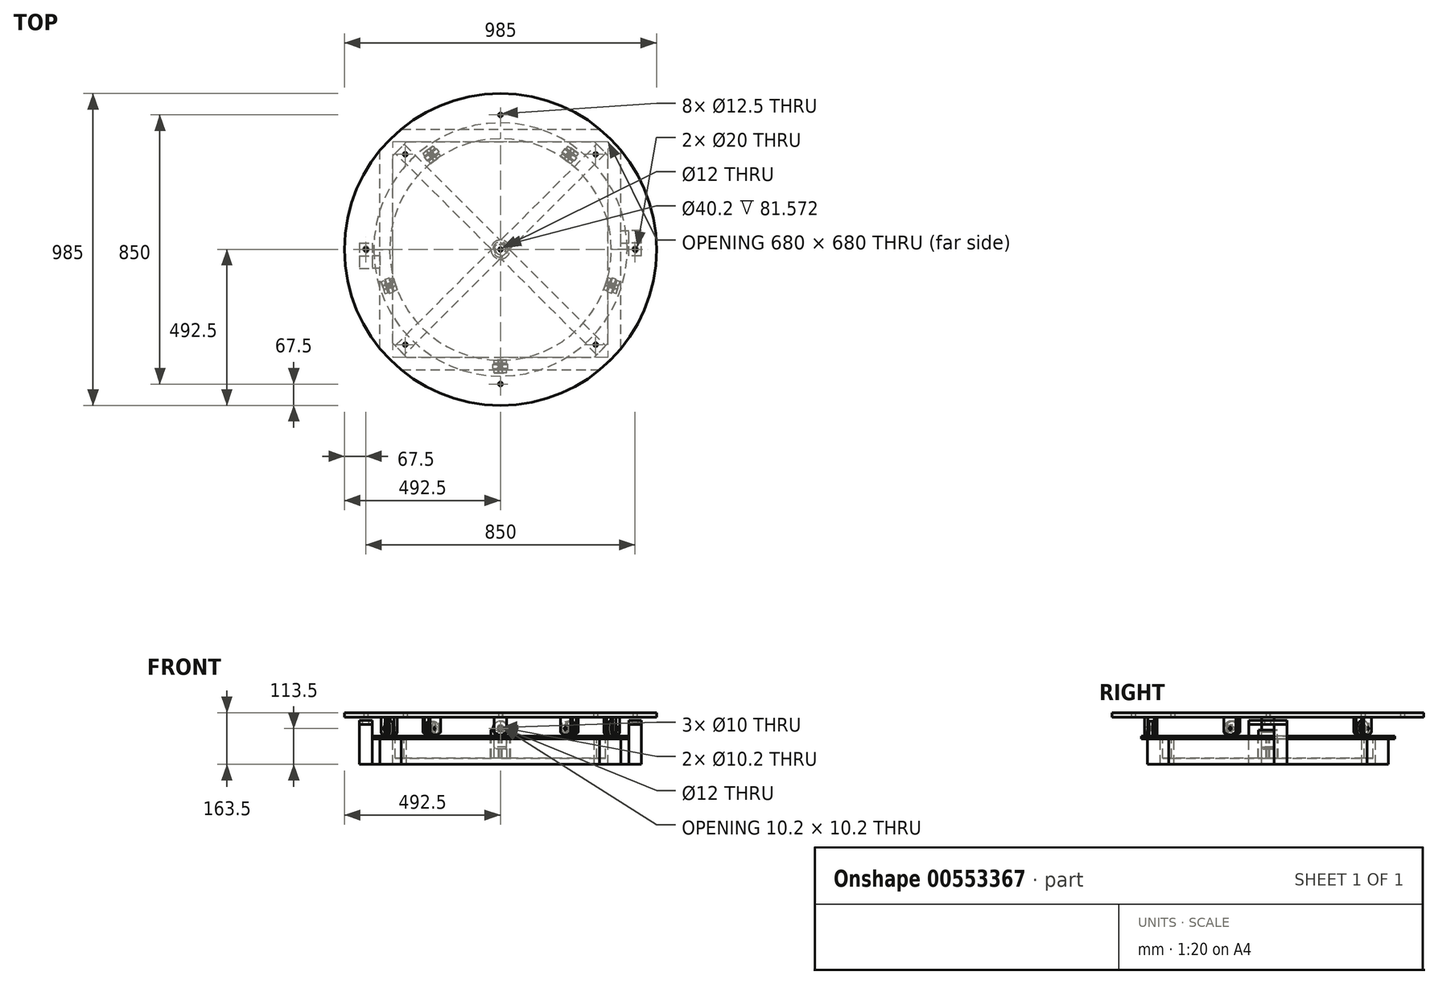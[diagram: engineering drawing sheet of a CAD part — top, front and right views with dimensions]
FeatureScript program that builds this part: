
annotation { "Feature Type Name" : "Feature", "Feature Type Description" : "" }
export const myFeature = defineFeature(function(context is Context, id is Id, definition is map)
    precondition{}
    {
        {
            var Q0;
            Q0=qCreatedBy(makeId("Top.planeOp"),FACE);
            var sketch = newSketch(context, id + "F0", { "sketchPlane" : qUnion([Q0])});
            skCircle(sketch, "E0", {"center": v(0, 0) * mm, "radius": 492.5 * mm});
            skCircle(sketch, "E1", {"center": v(0, -425) * mm, "radius": 6.25 * mm});
            skCircle(sketch, "E2.1.0", {"center": v(300.52, -300.52) * mm, "radius": 6.25 * mm});
            skCircle(sketch, "E2.2.0", {"center": v(425, 0) * mm, "radius": 6.25 * mm});
            skCircle(sketch, "E2.3.0", {"center": v(300.52, 300.52) * mm, "radius": 6.25 * mm});
            skCircle(sketch, "E2.4.0", {"center": v(0, 425) * mm, "radius": 6.25 * mm});
            skCircle(sketch, "E2.5.0", {"center": v(-300.52, 300.52) * mm, "radius": 6.25 * mm});
            skCircle(sketch, "E2.6.0", {"center": v(-425, 0) * mm, "radius": 6.25 * mm});
            skCircle(sketch, "E2.7.0", {"center": v(-300.52, -300.52) * mm, "radius": 6.25 * mm});
            skCircle(sketch, "E3", {"center": v(0, 0) * mm, "radius": 6 * mm});
            skSolve(sketch);
        }
        {
            var Q0;
            Q0 = qSketchRegion(id + "F0", true);
            extrude(context, id + "F1", {"entities" : qUnion([Q0]), "depth" : 15 * mm, "offsetDistance" : 25 * mm});
        }
        {
            var Q0;
            Q0=makeQuery(id+"F1.opExtrude","CAP_FACE",FACE,{"disambiguationData":[OSD([sQuery(id+"F0.wireOp",EDGE,"E0"),sQuery(id+"F0.wireOp",EDGE,"E1"),sQuery(id+"F0.wireOp",EDGE,"E2.1.0"),sQuery(id+"F0.wireOp",EDGE,"E2.2.0"),sQuery(id+"F0.wireOp",EDGE,"E2.3.0"),sQuery(id+"F0.wireOp",EDGE,"E2.4.0"),sQuery(id+"F0.wireOp",EDGE,"E2.5.0"),sQuery(id+"F0.wireOp",EDGE,"E2.6.0"),sQuery(id+"F0.wireOp",EDGE,"E2.7.0"),sQuery(id+"F0.wireOp",EDGE,"E3")])],"isStart":true});
            var sketch = newSketch(context, id + "F2", { "sketchPlane" : qUnion([Q0])});
            skCircle(sketch, "E4", {"center": v(0, 0) * mm, "radius": 390 * mm});
            skLineSegment(sketch, "E5", {"start": v(0, 389.49) * mm, "end": v(-20, 389.49) * mm});
            skLineSegment(sketch, "E6", {"start": v(0, 379.49) * mm, "end": v(-20, 379.49) * mm});
            skLineSegment(sketch, "E7", {"start": v(-20, 379.49) * mm, "end": v(-20, 389.49) * mm});
            skLineSegment(sketch, "E8.MirrorCS", {"start": v(0, 389.49) * mm, "end": v(20, 389.49) * mm});
            skLineSegment(sketch, "E9.MirrorCS", {"start": v(20, 379.49) * mm, "end": v(20, 399.5) * mm});
            skLineSegment(sketch, "E10.MirrorCS", {"start": v(0, 379.49) * mm, "end": v(20, 379.49) * mm});
            skLineSegment(sketch, "E11.0.1.0", {"start": v(0, 349.49) * mm, "end": v(20, 349.49) * mm});
            skLineSegment(sketch, "E11.0.1.1", {"start": v(20, 349.49) * mm, "end": v(20, 369.5) * mm});
            skLineSegment(sketch, "E11.0.1.2", {"start": v(0, 359.49) * mm, "end": v(20, 359.49) * mm});
            skLineSegment(sketch, "E11.0.1.3", {"start": v(0, 359.49) * mm, "end": v(-20, 359.49) * mm});
            skLineSegment(sketch, "E11.0.1.4", {"start": v(-20, 349.49) * mm, "end": v(-20, 359.49) * mm});
            skLineSegment(sketch, "E11.0.1.5", {"start": v(0, 349.49) * mm, "end": v(-20, 349.49) * mm});
            skLineSegment(sketch, "E11.direction1", {"start": v(0, 379.49) * mm, "end": v(15.32, 379.49) * mm, "construction": true});
            skLineSegment(sketch, "E11.direction2", {"start": v(0, 379.49) * mm, "end": v(0, 349.49) * mm, "construction": true});
            skLineSegment(sketch, "E12.1.0", {"start": v(-354.73, 136.29) * mm, "end": v(-373.77, 142.47) * mm});
            skLineSegment(sketch, "E12.1.1", {"start": v(-370.42, 120.36) * mm, "end": v(-364.24, 139.38) * mm});
            skLineSegment(sketch, "E12.1.2", {"start": v(-370.42, 120.36) * mm, "end": v(-376.6, 101.34) * mm});
            skLineSegment(sketch, "E12.1.3", {"start": v(-367.1, 98.25) * mm, "end": v(-376.6, 101.34) * mm});
            skLineSegment(sketch, "E12.1.4", {"start": v(-360.91, 117.27) * mm, "end": v(-367.1, 98.25) * mm});
            skLineSegment(sketch, "E12.1.5", {"start": v(-360.91, 117.27) * mm, "end": v(-356.18, 131.84) * mm, "construction": true});
            skLineSegment(sketch, "E12.1.6", {"start": v(-360.91, 117.27) * mm, "end": v(-332.38, 108) * mm, "construction": true});
            skLineSegment(sketch, "E12.1.7", {"start": v(-332.38, 108) * mm, "end": v(-326.2, 127.02) * mm});
            skLineSegment(sketch, "E12.1.8", {"start": v(-332.38, 108) * mm, "end": v(-338.56, 88.98) * mm});
            skLineSegment(sketch, "E12.1.9", {"start": v(-338.56, 88.98) * mm, "end": v(-348.07, 92.07) * mm});
            skLineSegment(sketch, "E12.1.10", {"start": v(-341.9, 111.09) * mm, "end": v(-348.07, 92.07) * mm});
            skLineSegment(sketch, "E12.1.11", {"start": v(-341.9, 111.09) * mm, "end": v(-335.71, 130.1) * mm});
            skLineSegment(sketch, "E12.1.12", {"start": v(-326.2, 127.02) * mm, "end": v(-345.23, 133.2) * mm});
            skLineSegment(sketch, "E12.1.13", {"start": v(-360.91, 117.27) * mm, "end": v(-354.73, 136.29) * mm});
            skLineSegment(sketch, "E12.2.0", {"start": v(-239.24, -295.26) * mm, "end": v(-251, -311.45) * mm});
            skLineSegment(sketch, "E12.2.1", {"start": v(-228.93, -315.1) * mm, "end": v(-245.11, -303.35) * mm});
            skLineSegment(sketch, "E12.2.2", {"start": v(-228.93, -315.1) * mm, "end": v(-212.75, -326.86) * mm});
            skLineSegment(sketch, "E12.2.3", {"start": v(-206.88, -318.77) * mm, "end": v(-212.75, -326.86) * mm});
            skLineSegment(sketch, "E12.2.4", {"start": v(-223.06, -307.01) * mm, "end": v(-206.88, -318.77) * mm});
            skLineSegment(sketch, "E12.2.5", {"start": v(-223.06, -307.01) * mm, "end": v(-235.45, -298) * mm, "construction": true});
            skLineSegment(sketch, "E12.2.6", {"start": v(-223.06, -307.01) * mm, "end": v(-205.42, -282.74) * mm, "construction": true});
            skLineSegment(sketch, "E12.2.7", {"start": v(-205.42, -282.74) * mm, "end": v(-221.6, -270.99) * mm});
            skLineSegment(sketch, "E12.2.8", {"start": v(-205.42, -282.74) * mm, "end": v(-189.24, -294.5) * mm});
            skLineSegment(sketch, "E12.2.9", {"start": v(-189.24, -294.5) * mm, "end": v(-195.12, -302.59) * mm});
            skLineSegment(sketch, "E12.2.10", {"start": v(-211.3, -290.83) * mm, "end": v(-195.12, -302.59) * mm});
            skLineSegment(sketch, "E12.2.11", {"start": v(-211.3, -290.83) * mm, "end": v(-227.48, -279.08) * mm});
            skLineSegment(sketch, "E12.2.12", {"start": v(-221.6, -270.99) * mm, "end": v(-233.37, -287.18) * mm});
            skLineSegment(sketch, "E12.2.13", {"start": v(-223.06, -307.01) * mm, "end": v(-239.24, -295.26) * mm});
            skLineSegment(sketch, "E12.3.0", {"start": v(206.88, -318.77) * mm, "end": v(218.64, -334.96) * mm});
            skLineSegment(sketch, "E12.3.1", {"start": v(228.93, -315.1) * mm, "end": v(212.75, -326.86) * mm});
            skLineSegment(sketch, "E12.3.2", {"start": v(228.93, -315.1) * mm, "end": v(245.11, -303.35) * mm});
            skLineSegment(sketch, "E12.3.3", {"start": v(239.24, -295.26) * mm, "end": v(245.11, -303.35) * mm});
            skLineSegment(sketch, "E12.3.4", {"start": v(223.06, -307.01) * mm, "end": v(239.24, -295.26) * mm});
            skLineSegment(sketch, "E12.3.5", {"start": v(223.06, -307.01) * mm, "end": v(210.66, -316.02) * mm, "construction": true});
            skLineSegment(sketch, "E12.3.6", {"start": v(223.06, -307.01) * mm, "end": v(205.42, -282.74) * mm, "construction": true});
            skLineSegment(sketch, "E12.3.7", {"start": v(205.42, -282.74) * mm, "end": v(189.24, -294.5) * mm});
            skLineSegment(sketch, "E12.3.8", {"start": v(205.42, -282.74) * mm, "end": v(221.6, -270.99) * mm});
            skLineSegment(sketch, "E12.3.9", {"start": v(221.6, -270.99) * mm, "end": v(227.48, -279.08) * mm});
            skLineSegment(sketch, "E12.3.10", {"start": v(211.3, -290.83) * mm, "end": v(227.48, -279.08) * mm});
            skLineSegment(sketch, "E12.3.11", {"start": v(211.3, -290.83) * mm, "end": v(195.12, -302.59) * mm});
            skLineSegment(sketch, "E12.3.12", {"start": v(189.24, -294.5) * mm, "end": v(201, -310.69) * mm});
            skLineSegment(sketch, "E12.3.13", {"start": v(223.06, -307.01) * mm, "end": v(206.88, -318.77) * mm});
            skLineSegment(sketch, "E12.4.0", {"start": v(367.1, 98.25) * mm, "end": v(386.13, 104.43) * mm});
            skLineSegment(sketch, "E12.4.1", {"start": v(370.42, 120.36) * mm, "end": v(376.6, 101.34) * mm});
            skLineSegment(sketch, "E12.4.2", {"start": v(370.42, 120.36) * mm, "end": v(364.24, 139.38) * mm});
            skLineSegment(sketch, "E12.4.3", {"start": v(354.73, 136.29) * mm, "end": v(364.24, 139.38) * mm});
            skLineSegment(sketch, "E12.4.4", {"start": v(360.91, 117.27) * mm, "end": v(354.73, 136.29) * mm});
            skLineSegment(sketch, "E12.4.5", {"start": v(360.91, 117.27) * mm, "end": v(365.65, 102.7) * mm, "construction": true});
            skLineSegment(sketch, "E12.4.6", {"start": v(360.91, 117.27) * mm, "end": v(332.38, 108) * mm, "construction": true});
            skLineSegment(sketch, "E12.4.7", {"start": v(332.38, 108) * mm, "end": v(338.56, 88.98) * mm});
            skLineSegment(sketch, "E12.4.8", {"start": v(332.38, 108) * mm, "end": v(326.2, 127.02) * mm});
            skLineSegment(sketch, "E12.4.9", {"start": v(326.2, 127.02) * mm, "end": v(335.71, 130.1) * mm});
            skLineSegment(sketch, "E12.4.10", {"start": v(341.9, 111.09) * mm, "end": v(335.71, 130.1) * mm});
            skLineSegment(sketch, "E12.4.11", {"start": v(341.9, 111.09) * mm, "end": v(348.07, 92.07) * mm});
            skLineSegment(sketch, "E12.4.12", {"start": v(338.56, 88.98) * mm, "end": v(357.6, 95.16) * mm});
            skLineSegment(sketch, "E12.4.13", {"start": v(360.91, 117.27) * mm, "end": v(367.1, 98.25) * mm});
            skSolve(sketch);
        }
        {
            var Q0;
            Q0=makeQuery(id+"F2.imprint","IMPRINT",FACE,{"disambiguationData":[TD([[makeQuery(id+"F2.imprint","IMPRINT",EDGE,{"derivedFrom":sQuery(id+"F2.wireOp",EDGE,"E5")}),1.0]])]});
            var Q1;
            Q1=makeQuery(id+"F2.imprint","IMPRINT",FACE,{"disambiguationData":[TD([[makeQuery(id+"F2.imprint","IMPRINT",EDGE,{"derivedFrom":sQuery(id+"F2.wireOp",EDGE,"E11.0.1.0")}),1.0]])]});
            extrude(context, id + "F3", {"entities" : qUnion([Q0, Q1]), "depth" : 55 * mm, "offsetDistance" : 25 * mm});
        }
        {
            var Q0;
            Q0=makeQuery(id+"F3.opExtrude","SWEPT_FACE",FACE,{"disambiguationData":[OSD([sQuery(id+"F2.wireOp",EDGE,"E11.0.1.0"),sQuery(id+"F2.wireOp",EDGE,"E11.0.1.5")])]});
            var sketch = newSketch(context, id + "F4", { "sketchPlane" : qUnion([Q0])});
            skCircle(sketch, "E13", {"center": v(0, -35) * mm, "radius": 5.1 * mm});
            skLineSegment(sketch, "E14", {"start": v(20, -47.5) * mm, "end": v(7, -55) * mm});
            skLineSegment(sketch, "E15", {"start": v(7, -55) * mm, "end": v(-7, -55) * mm});
            skLineSegment(sketch, "E16", {"start": v(-7, -55) * mm, "end": v(-20, -47.5) * mm});
            skLineSegment(sketch, "E17", {"start": v(-20, -47.5) * mm, "end": v(-20, -55) * mm});
            skLineSegment(sketch, "E18", {"start": v(-20, -55) * mm, "end": v(20, -55) * mm});
            skLineSegment(sketch, "E19", {"start": v(20, -55) * mm, "end": v(20, -47.5) * mm});
            skSolve(sketch);
        }
        {
            var Q0;
            Q0 = qSketchRegion(id + "F4", true);
            extrude(context, id + "F5", {"entities" : qUnion([Q0]), "operationType" : NewBodyOperationType.REMOVE, "endBound" : BoundingType.THROUGH_ALL, "oppositeDirection" : true, "depth" : 25 * mm, "offsetDistance" : 25 * mm});
        }
        {
            var Q0;
            Q0=makeQuery(id+"F3.opExtrude","SWEPT_BODY",BODY,{"disambiguationData":[OSD([sQuery(id+"F2.wireOp",EDGE,"E11.0.1.0"),sQuery(id+"F2.wireOp",EDGE,"E11.0.1.1"),sQuery(id+"F2.wireOp",EDGE,"E11.0.1.2"),sQuery(id+"F2.wireOp",EDGE,"E11.0.1.3"),sQuery(id+"F2.wireOp",EDGE,"E11.0.1.4"),sQuery(id+"F2.wireOp",EDGE,"E11.0.1.5")])]});
            var Q1;
            Q1=makeQuery(id+"F3.opExtrude","SWEPT_BODY",BODY,{"disambiguationData":[OSD([sQuery(id+"F2.wireOp",EDGE,"E5"),sQuery(id+"F2.wireOp",EDGE,"E6"),sQuery(id+"F2.wireOp",EDGE,"E7"),sQuery(id+"F2.wireOp",EDGE,"E8.MirrorCS"),sQuery(id+"F2.wireOp",EDGE,"E9.MirrorCS"),sQuery(id+"F2.wireOp",EDGE,"E10.MirrorCS")])]});
            var Q2;
            Q2=makeQuery(id+"F1.opExtrude","CAP_EDGE",EDGE,{"disambiguationData":[OSD([sQuery(id+"F0.wireOp",EDGE,"E3")])],"isStart":true});
            circularPattern(context, id + "F6", {"entities" : qUnion([Q0, Q1]), "axis" : qUnion([Q2]), "angle" : 360 * degree, "instanceCount" : 5, "equalSpace" : true});
        }
        {
            var Q0;
            Q0=qCreatedBy(makeId("Front.planeOp"),FACE);
            var sketch = newSketch(context, id + "F7", { "sketchPlane" : qUnion([Q0])});
            skLineSegment(sketch, "E20", {"start": v(0, 15) * mm, "end": v(0, -100) * mm});
            skLineSegment(sketch, "E21", {"start": v(0, -100) * mm, "end": v(16, -100) * mm});
            skLineSegment(sketch, "E22", {"start": v(20, -93.07) * mm, "end": v(20, 0) * mm});
            skLineSegment(sketch, "E23", {"start": v(20, 0) * mm, "end": v(6, 0) * mm});
            skLineSegment(sketch, "E24", {"start": v(6, 0) * mm, "end": v(6, 15) * mm});
            skLineSegment(sketch, "E25", {"start": v(6, 15) * mm, "end": v(0, 15) * mm});
            skLineSegment(sketch, "E26", {"start": v(16, -100) * mm, "end": v(20, -93.07) * mm});
            skSolve(sketch);
        }
        {
            var Q0;
            Q0 = qSketchRegion(id + "F7", true);
            var Q1;
            Q1=sQuery(id+"F7.wireOp",EDGE,"E20");
            revolve(context, id + "F8", {"entities" : qUnion([Q0]), "axis" : qUnion([Q1]), "revolveType" : RevolveType.FULL});
        }
        {
            var Q0;
            Q0=makeQuery(id+"F3.opExtrude","SWEPT_FACE",FACE,{"disambiguationData":[OSD([sQuery(id+"F2.wireOp",EDGE,"E11.0.1.2"),sQuery(id+"F2.wireOp",EDGE,"E11.0.1.3")])]});
            var sketch = newSketch(context, id + "F9", { "sketchPlane" : qUnion([Q0])});
            skCircle(sketch, "E27", {"center": v(0, -35) * mm, "radius": 23.5 * mm});
            skCircle(sketch, "E28", {"center": v(0, -35) * mm, "radius": 6 * mm});
            skSolve(sketch);
        }
        {
            var Q0;
            Q0 = qSketchRegion(id + "F9", true);
            extrude(context, id + "F10", {"entities" : qUnion([Q0]), "depth" : 17 * mm, "offsetDistance" : 25 * mm, "hasSecondDirection" : true, "secondDirectionOppositeDirection" : false, "secondDirectionDepth" : 3 * mm});
        }
        {
            var Q0;
            Q0=makeQuery(id+"F10.opExtrude","CAP_EDGE",EDGE,{"disambiguationData":[OSD([sQuery(id+"F9.wireOp",EDGE,"E27")])],"isStart":false});
            var Q1;
            {var subQ0=sQuery(id+"F9.wireOp",EDGE,"E27");var subQ1=makeQuery(id+"F10.opExtrude","SWEPT_FACE",FACE,{"disambiguationData":[OSD([subQ0])]});var subQ2=makeQuery(id+"F10.opExtrude","CAP_FACE",FACE,{"disambiguationData":[OSD([subQ0,sQuery(id+"F9.wireOp",EDGE,"E28")])],"isStart":true});Q1=makeQuery(id+"F10.boolean.opBoolean","SPLIT",EDGE,{"disambiguationData":[topologyDisambiguationEdgeConnected([subQ1,subQ2]),TD([makeQuery(id+"F3.opExtrude","SWEPT_FACE",FACE,{"disambiguationData":[OSD([sQuery(id+"F2.wireOp",EDGE,"E11.0.1.1")])]})])],"derivedFrom":makeQuery(id+"F10.opExtrude","CAP_EDGE",EDGE,{"disambiguationData":[OSD([subQ0])],"isStart":true})});}
            var Q2;
            {var subQ1=sQuery(id+"F2.wireOp",EDGE,"E11.0.1.4");var subQ9=sQuery(id+"F9.wireOp",EDGE,"E27");var subQ10=makeQuery(id+"F10.opExtrude","SWEPT_FACE",FACE,{"disambiguationData":[OSD([subQ9])]});var subQ11=makeQuery(id+"F10.opExtrude","CAP_FACE",FACE,{"disambiguationData":[OSD([subQ9,sQuery(id+"F9.wireOp",EDGE,"E28")])],"isStart":true});Q2=makeQuery(id+"F10.boolean.opBoolean","SPLIT",EDGE,{"disambiguationData":[topologyDisambiguationEdgeConnected([subQ10,subQ11]),TD([makeQuery(id+"F5.boolean.opBoolean","COPY",FACE,{"disambiguationData":[TD([makeQuery(id+"F3.opExtrude","SWEPT_FACE",FACE,{"disambiguationData":[OSD([subQ1])]})])],"derivedFrom":makeQuery(id+"F5.opExtrude","SWEPT_FACE",FACE,{"disambiguationData":[OSD([sQuery(id+"F4.wireOp",EDGE,"E14")])]})})])],"derivedFrom":makeQuery(id+"F10.opExtrude","CAP_EDGE",EDGE,{"disambiguationData":[OSD([subQ9])],"isStart":true})});}
            var Q3;
            {var subQ0=sQuery(id+"F9.wireOp",EDGE,"E27");var subQ1=makeQuery(id+"F10.opExtrude","SWEPT_FACE",FACE,{"disambiguationData":[OSD([subQ0])]});var subQ2=makeQuery(id+"F10.opExtrude","CAP_FACE",FACE,{"disambiguationData":[OSD([subQ0,sQuery(id+"F9.wireOp",EDGE,"E28")])],"isStart":true});Q3=makeQuery(id+"F10.boolean.opBoolean","SPLIT",EDGE,{"disambiguationData":[topologyDisambiguationEdgeConnected([subQ1,subQ2]),TD([makeQuery(id+"F3.opExtrude","SWEPT_FACE",FACE,{"disambiguationData":[OSD([sQuery(id+"F2.wireOp",EDGE,"E11.0.1.4")])]})])],"derivedFrom":makeQuery(id+"F10.opExtrude","CAP_EDGE",EDGE,{"disambiguationData":[OSD([subQ0])],"isStart":true})});}
            chamfer(context, id + "F11", {"entities" : qUnion([Q0, Q1, Q2, Q3]), "width" : 1 * mm, "tangentPropagation" : true});
        }
        {
            var Q0;
            Q0=makeQuery(id+"F10.opExtrude","SWEPT_BODY",BODY,{"disambiguationData":[OSD([sQuery(id+"F9.wireOp",EDGE,"E27"),sQuery(id+"F9.wireOp",EDGE,"E28")])]});
            var Q1;
            Q1=makeQuery(id+"F8.opRevolve","SWEPT_FACE",FACE,{"disambiguationData":[OSD([sQuery(id+"F7.wireOp",EDGE,"E22")])]});
            circularPattern(context, id + "F12", {"entities" : qUnion([Q0]), "axis" : qUnion([Q1]), "angle" : 360 * degree, "instanceCount" : 5, "equalSpace" : true});
        }
        {
            var Q0;
            Q0=makeQuery(id+"F1.opExtrude","CAP_FACE",FACE,{"disambiguationData":[OSD([sQuery(id+"F0.wireOp",EDGE,"E0"),sQuery(id+"F0.wireOp",EDGE,"E1"),sQuery(id+"F0.wireOp",EDGE,"E2.1.0"),sQuery(id+"F0.wireOp",EDGE,"E2.2.0"),sQuery(id+"F0.wireOp",EDGE,"E2.3.0"),sQuery(id+"F0.wireOp",EDGE,"E2.4.0"),sQuery(id+"F0.wireOp",EDGE,"E2.5.0"),sQuery(id+"F0.wireOp",EDGE,"E2.6.0"),sQuery(id+"F0.wireOp",EDGE,"E2.7.0"),sQuery(id+"F0.wireOp",EDGE,"E3")])],"isStart":true});
            cPlane(context, id + "F13", {"entities" : qUnion([Q0]), "cplaneType" : CPlaneType.OFFSET, "offset" : 58.5 * mm, "width" : 150 * mm, "height" : 150 * mm});
        }
        {
            var Q0;
            Q0=qCreatedBy(id+"F13.planeOp",FACE);
            var sketch = newSketch(context, id + "F14", { "sketchPlane" : qUnion([Q0])});
            skArc(sketch, "E29", {"start": v(400, 0.1) * mm, "mid": v(0, 400) * mm, "end": v(-400, 0.1) * mm});
            skArc(sketch, "E30", {"start": v(350, 0.1) * mm, "mid": v(0, 350) * mm, "end": v(-350, 0.1) * mm});
            skLineSegment(sketch, "E31", {"start": v(350, 0) * mm, "end": v(400, 0) * mm});
            skPoint(sketch, "E32.endSnap0", {"position": v(375, 0) * mm});
            skLineSegment(sketch, "E33", {"start": v(-350, 0) * mm, "end": v(-400, 0) * mm});
            skLineSegment(sketch, "E34", {"start": v(400, -0.1) * mm, "end": v(350, -0.1) * mm});
            skLineSegment(sketch, "E35.MirrorCS", {"start": v(400, 0.1) * mm, "end": v(350, 0.1) * mm});
            skLineSegment(sketch, "E36.1.0", {"start": v(-400, 0.1) * mm, "end": v(-350, 0.1) * mm});
            skLineSegment(sketch, "E36.1.1", {"start": v(-400, -0.1) * mm, "end": v(-350, -0.1) * mm});
            skArc(sketch, "E37.trimOffspring", {"start": v(-400, -0.1) * mm, "mid": v(0, -400) * mm, "end": v(400, -0.1) * mm});
            skArc(sketch, "E38.trimOffspring", {"start": v(-350, -0.1) * mm, "mid": v(0, -350) * mm, "end": v(350, -0.1) * mm});
            skSolve(sketch);
        }
        {
            var Q0;
            Q0=makeQuery(id+"F14.imprint","IMPRINT",FACE,{"disambiguationData":[TD([[makeQuery(id+"F14.imprint","IMPRINT",EDGE,{"derivedFrom":sQuery(id+"F14.wireOp",EDGE,"E34")}),1.0]])]});
            var Q1;
            Q1=makeQuery(id+"F14.imprint","IMPRINT",FACE,{"disambiguationData":[TD([[makeQuery(id+"F14.imprint","IMPRINT",EDGE,{"derivedFrom":sQuery(id+"F14.wireOp",EDGE,"E29")}),1.0]])]});
            extrude(context, id + "F15", {"entities" : qUnion([Q0, Q1]), "depth" : 10 * mm, "offsetDistance" : 25 * mm});
        }
        {
            var Q0;
            Q0=qCreatedBy(makeId("Front.planeOp"),FACE);
            var sketch = newSketch(context, id + "F16", { "sketchPlane" : qUnion([Q0])});
            skLineSegment(sketch, "E39", {"start": v(20.1, -46.93) * mm, "end": v(20.1, -128.5) * mm});
            skLineSegment(sketch, "E40", {"start": v(20.1, -128.5) * mm, "end": v(30, -128.5) * mm});
            skLineSegment(sketch, "E41", {"start": v(30, -128.5) * mm, "end": v(30, -40) * mm});
            skLineSegment(sketch, "E42", {"start": v(30, -40) * mm, "end": v(24.1, -40) * mm});
            skLineSegment(sketch, "E43", {"start": v(24.1, -40) * mm, "end": v(20.1, -46.93) * mm});
            skLineSegment(sketch, "E44", {"start": v(0, -24.97) * mm, "end": v(0, -84.03) * mm});
            skSolve(sketch);
        }
        {
            var Q0;
            Q0=makeQuery(id+"F16.imprint","IMPRINT",FACE,{"disambiguationData":[TD([[makeQuery(id+"F16.imprint","IMPRINT",EDGE,{"derivedFrom":sQuery(id+"F16.wireOp",EDGE,"E39")}),1.0]])]});
            var Q1;
            Q1=sQuery(id+"F16.wireOp",EDGE,"E44");
            revolve(context, id + "F17", {"entities" : qUnion([Q0]), "axis" : qUnion([Q1]), "revolveType" : RevolveType.FULL});
        }
        {
            var Q0;
            Q0=makeQuery(id+"F15.opExtrude","CAP_FACE",FACE,{"disambiguationData":[OSD([sQuery(id+"F14.wireOp",EDGE,"E29"),sQuery(id+"F14.wireOp",EDGE,"E30"),sQuery(id+"F14.wireOp",EDGE,"E35.MirrorCS"),sQuery(id+"F14.wireOp",EDGE,"E36.1.0")])],"isStart":false});
            var sketch = newSketch(context, id + "F18", { "sketchPlane" : qUnion([Q0])});
            skPoint(sketch, "E45.firstSnap0", {"position": v(0, 400) * mm});
            skLineSegment(sketch, "E45.bottom", {"start": v(-312.96, 380) * mm, "end": v(312.96, 380) * mm});
            skLineSegment(sketch, "E45.top", {"start": v(-312.96, -380) * mm, "end": v(312.96, -380) * mm});
            skLineSegment(sketch, "E45.left", {"start": v(-380, 312.96) * mm, "end": v(-380, -312.96) * mm});
            skLineSegment(sketch, "E45.right", {"start": v(380, 312.96) * mm, "end": v(380, -312.96) * mm});
            skLineSegment(sketch, "E46.0", {"start": v(-296.4, 340) * mm, "end": v(296.4, 340) * mm});
            skLineSegment(sketch, "E46.1", {"start": v(-340, 296.4) * mm, "end": v(-340, -296.4) * mm});
            skLineSegment(sketch, "E47", {"start": v(-332.34, 304.06) * mm, "end": v(-31.62, 3.34) * mm});
            skLineSegment(sketch, "E48", {"start": v(332.34, -304.06) * mm, "end": v(31.62, -3.34) * mm});
            skLineSegment(sketch, "E49", {"start": v(304.06, 332.34) * mm, "end": v(3.34, 31.62) * mm});
            skLineSegment(sketch, "E50", {"start": v(-304.06, -332.34) * mm, "end": v(-3.34, -31.62) * mm});
            skCircle(sketch, "E51", {"center": v(0, 0) * mm, "radius": 30 * mm});
            skLineSegment(sketch, "E52.trimOffspring", {"start": v(3.34, -31.62) * mm, "end": v(304.06, -332.34) * mm});
            skLineSegment(sketch, "E53.trimOffspring", {"start": v(31.62, 3.34) * mm, "end": v(332.34, 304.06) * mm});
            skLineSegment(sketch, "E54.trimOffspring", {"start": v(-3.34, 31.62) * mm, "end": v(-304.06, 332.34) * mm});
            skLineSegment(sketch, "E55.trimOffspring", {"start": v(-31.62, -3.34) * mm, "end": v(-332.34, -304.06) * mm});
            skPoint(sketch, "E56.orphan", {"position": v(-380, 400) * mm});
            skPoint(sketch, "E57.orphan", {"position": v(-340, 340) * mm});
            skLineSegment(sketch, "E58", {"start": v(-312.96, 380) * mm, "end": v(-380, 312.96) * mm});
            skLineSegment(sketch, "E59.0", {"start": v(-296.4, 340) * mm, "end": v(-340, 296.4) * mm});
            skLineSegment(sketch, "E60.1.0", {"start": v(-380, -312.96) * mm, "end": v(-312.96, -380) * mm});
            skLineSegment(sketch, "E60.1.1", {"start": v(-340, -296.4) * mm, "end": v(-296.4, -340) * mm});
            skLineSegment(sketch, "E60.2.0", {"start": v(312.96, -380) * mm, "end": v(380, -312.96) * mm});
            skLineSegment(sketch, "E60.2.1", {"start": v(296.4, -340) * mm, "end": v(340, -296.4) * mm});
            skLineSegment(sketch, "E60.3.0", {"start": v(380, 312.96) * mm, "end": v(312.96, 380) * mm});
            skLineSegment(sketch, "E60.3.1", {"start": v(340, 296.4) * mm, "end": v(296.4, 340) * mm});
            skPoint(sketch, "E61.orphan", {"position": v(350, 321.72) * mm});
            skLineSegment(sketch, "E62.trimOffspring", {"start": v(340, 296.4) * mm, "end": v(340, -296.4) * mm});
            skPoint(sketch, "E63.trimOffspring.end.orphan", {"position": v(350.45, 350.45) * mm});
            skPoint(sketch, "E64.orphan", {"position": v(350, -321.72) * mm});
            skLineSegment(sketch, "E65.trimOffspring", {"start": v(-296.4, -340) * mm, "end": v(296.4, -340) * mm});
            skLineSegment(sketch, "E66", {"start": v(31.62, -3.34) * mm, "end": v(29.5, -5.46) * mm});
            skLineSegment(sketch, "E67", {"start": v(3.34, -31.62) * mm, "end": v(5.46, -29.5) * mm});
            skLineSegment(sketch, "E68.1.0", {"start": v(3.34, 31.62) * mm, "end": v(5.46, 29.5) * mm});
            skLineSegment(sketch, "E68.1.1", {"start": v(31.62, 3.34) * mm, "end": v(29.5, 5.46) * mm});
            skLineSegment(sketch, "E68.2.0", {"start": v(-31.62, 3.34) * mm, "end": v(-29.5, 5.46) * mm});
            skLineSegment(sketch, "E68.2.1", {"start": v(-3.34, 31.62) * mm, "end": v(-5.46, 29.5) * mm});
            skLineSegment(sketch, "E68.3.0", {"start": v(-3.34, -31.62) * mm, "end": v(-5.46, -29.5) * mm});
            skLineSegment(sketch, "E68.3.1", {"start": v(-31.62, -3.34) * mm, "end": v(-29.5, -5.46) * mm});
            skSolve(sketch);
        }
        {
            var Q0;
            Q0=makeQuery(id+"F18.imprint","IMPRINT",FACE,{"disambiguationData":[TD([[makeQuery(id+"F18.imprint","IMPRINT",EDGE,{"derivedFrom":sQuery(id+"F18.wireOp",EDGE,"E45.top")}),1.0]])]});
            var Q1;
            {var subQ0=sQuery(id+"F18.wireOp",EDGE,"E46.0");var subQ1=makeQuery(id+"F15.opExtrude","CAP_EDGE",EDGE,{"disambiguationData":[OSD([sQuery(id+"F14.wireOp",EDGE,"E29")])],"isStart":false});var subQ2=makeQuery(id+"F18.imprint","INTERSECT",VERTEX,{"disambiguationData":[OD(0.0)],"derivedFrom":[subQ1,subQ0]});Q1=makeQuery(id+"F18.imprint","IMPRINT",FACE,{"disambiguationData":[TD([[makeQuery(id+"F18.imprint","IMPRINT",EDGE,{"disambiguationData":[TD([[subQ2,-1.0]])],"derivedFrom":subQ0}),1.0]])]});}
            var Q2;
            {var subQ0=sQuery(id+"F18.wireOp",EDGE,"E60.3.0");Q2=makeQuery(id+"F18.imprint","IMPRINT",FACE,{"disambiguationData":[TD([[makeQuery(id+"F18.imprint","IMPRINT",EDGE,{"derivedFrom":subQ0}),1.0]])]});}
            var Q3;
            {var subQ5=makeQuery(id+"F15.opExtrude","CAP_EDGE",EDGE,{"disambiguationData":[OSD([sQuery(id+"F14.wireOp",EDGE,"E29")])],"isStart":false});var subQ7=sQuery(id+"F18.wireOp",EDGE,"E45.left");var subQ8=makeQuery(id+"F18.imprint","INTERSECT",VERTEX,{"derivedFrom":[subQ5,subQ7]});Q3=makeQuery(id+"F18.imprint","IMPRINT",FACE,{"disambiguationData":[TD([[makeQuery(id+"F18.imprint","IMPRINT",EDGE,{"disambiguationData":[TD([[subQ8,-1.0]])],"derivedFrom":subQ7}),1.0]])]});}
            var Q4;
            {var subQ0=sQuery(id+"F18.wireOp",EDGE,"E58");Q4=makeQuery(id+"F18.imprint","IMPRINT",FACE,{"disambiguationData":[TD([[makeQuery(id+"F18.imprint","IMPRINT",EDGE,{"derivedFrom":subQ0}),1.0]])]});}
            var Q5;
            {var subQ5=makeQuery(id+"F15.opExtrude","CAP_EDGE",EDGE,{"disambiguationData":[OSD([sQuery(id+"F14.wireOp",EDGE,"E29")])],"isStart":false});var subQ7=sQuery(id+"F18.wireOp",EDGE,"E45.right");var subQ9=makeQuery(id+"F18.imprint","INTERSECT",VERTEX,{"derivedFrom":[subQ5,subQ7]});Q5=makeQuery(id+"F18.imprint","IMPRINT",FACE,{"disambiguationData":[TD([[makeQuery(id+"F18.imprint","IMPRINT",EDGE,{"disambiguationData":[TD([[subQ9,-1.0]])],"derivedFrom":subQ7}),-1.0]])]});}
            var Q6;
            {var subQ0=sQuery(id+"F18.wireOp",EDGE,"E46.0");var subQ1=makeQuery(id+"F15.opExtrude","CAP_EDGE",EDGE,{"disambiguationData":[OSD([sQuery(id+"F14.wireOp",EDGE,"E30")])],"isStart":false});var subQ2=makeQuery(id+"F18.imprint","INTERSECT",VERTEX,{"disambiguationData":[OD(0.0)],"derivedFrom":[subQ1,subQ0]});Q6=makeQuery(id+"F18.imprint","IMPRINT",FACE,{"disambiguationData":[TD([[makeQuery(id+"F18.imprint","IMPRINT",EDGE,{"disambiguationData":[TD([[subQ2,-1.0]])],"derivedFrom":subQ0}),1.0]])]});}
            extrude(context, id + "F19", {"entities" : qUnion([Q0, Q1, Q2, Q3, Q4, Q5, Q6]), "depth" : 80 * mm, "offsetDistance" : 25 * mm});
        }
        {
            var Q0;
            {var subQ0=sQuery(id+"F18.wireOp",EDGE,"E51");var subQ1=sQuery(id+"F18.wireOp",EDGE,"E47");var subQ2=makeQuery(id+"F18.imprint","INTERSECT",VERTEX,{"derivedFrom":[subQ1,subQ0]});Q0=makeQuery(id+"F18.imprint","IMPRINT",FACE,{"disambiguationData":[TD([[makeQuery(id+"F18.imprint","IMPRINT",EDGE,{"disambiguationData":[TD([[subQ2,1.0]])],"derivedFrom":subQ1}),1.0]])]});}
            var Q1;
            {var subQ0=sQuery(id+"F18.wireOp",EDGE,"E47");var subQ1=makeQuery(id+"F15.opExtrude","CAP_EDGE",EDGE,{"disambiguationData":[OSD([sQuery(id+"F14.wireOp",EDGE,"E29")])],"isStart":false});var subQ2=makeQuery(id+"F18.imprint","INTERSECT",VERTEX,{"derivedFrom":[subQ1,subQ0]});Q1=makeQuery(id+"F18.imprint","IMPRINT",FACE,{"disambiguationData":[TD([[makeQuery(id+"F18.imprint","IMPRINT",EDGE,{"disambiguationData":[TD([[subQ2,-1.0]])],"derivedFrom":subQ0}),1.0]])]});}
            var Q2;
            {var subQ0=sQuery(id+"F18.wireOp",EDGE,"E51");var subQ1=sQuery(id+"F18.wireOp",EDGE,"E49");var subQ2=makeQuery(id+"F18.imprint","INTERSECT",VERTEX,{"derivedFrom":[subQ1,subQ0]});Q2=makeQuery(id+"F18.imprint","IMPRINT",FACE,{"disambiguationData":[TD([[makeQuery(id+"F18.imprint","IMPRINT",EDGE,{"disambiguationData":[TD([[subQ2,1.0]])],"derivedFrom":subQ1}),1.0]])]});}
            var Q3;
            {var subQ0=sQuery(id+"F18.wireOp",EDGE,"E49");var subQ1=makeQuery(id+"F15.opExtrude","CAP_EDGE",EDGE,{"disambiguationData":[OSD([sQuery(id+"F14.wireOp",EDGE,"E29")])],"isStart":false});var subQ2=makeQuery(id+"F18.imprint","INTERSECT",VERTEX,{"derivedFrom":[subQ1,subQ0]});Q3=makeQuery(id+"F18.imprint","IMPRINT",FACE,{"disambiguationData":[TD([[makeQuery(id+"F18.imprint","IMPRINT",EDGE,{"disambiguationData":[TD([[subQ2,-1.0]])],"derivedFrom":subQ0}),1.0]])]});}
            var Q4;
            {var subQ0=sQuery(id+"F18.wireOp",EDGE,"E48");Q4=makeQuery(id+"F18.imprint","IMPRINT",FACE,{"disambiguationData":[TD([[makeQuery(id+"F18.imprint","IMPRINT",EDGE,{"derivedFrom":subQ0}),1.0]])]});}
            var Q5;
            {var subQ0=sQuery(id+"F18.wireOp",EDGE,"E50");Q5=makeQuery(id+"F18.imprint","IMPRINT",FACE,{"disambiguationData":[TD([[makeQuery(id+"F18.imprint","IMPRINT",EDGE,{"derivedFrom":subQ0}),1.0]])]});}
            var Q6;
            {var subQ0=sQuery(id+"F18.wireOp",EDGE,"E59.0");var subQ1=sQuery(id+"F18.wireOp",EDGE,"E47");var subQ2=makeQuery(id+"F18.imprint","INTERSECT",VERTEX,{"derivedFrom":[subQ1,subQ0]});Q6=makeQuery(id+"F18.imprint","IMPRINT",FACE,{"disambiguationData":[TD([[makeQuery(id+"F18.imprint","IMPRINT",EDGE,{"disambiguationData":[TD([[subQ2,-1.0]])],"derivedFrom":subQ1}),1.0]])]});}
            var Q7;
            {var subQ0=sQuery(id+"F18.wireOp",EDGE,"E60.3.1");var subQ1=sQuery(id+"F18.wireOp",EDGE,"E49");var subQ2=makeQuery(id+"F18.imprint","INTERSECT",VERTEX,{"derivedFrom":[subQ1,subQ0]});Q7=makeQuery(id+"F18.imprint","IMPRINT",FACE,{"disambiguationData":[TD([[makeQuery(id+"F18.imprint","IMPRINT",EDGE,{"disambiguationData":[TD([[subQ2,-1.0]])],"derivedFrom":subQ1}),1.0]])]});}
            var Q8;
            {var subQ0=sQuery(id+"F18.wireOp",EDGE,"E68.2.0");Q8=makeQuery(id+"F18.imprint","IMPRINT",FACE,{"disambiguationData":[TD([[makeQuery(id+"F18.imprint","IMPRINT",EDGE,{"derivedFrom":subQ0}),1.0]])]});}
            var Q9;
            {var subQ4=sQuery(id+"F18.wireOp",EDGE,"E68.1.0");Q9=makeQuery(id+"F18.imprint","IMPRINT",FACE,{"disambiguationData":[TD([[makeQuery(id+"F18.imprint","IMPRINT",EDGE,{"derivedFrom":subQ4}),1.0]])]});}
            extrude(context, id + "F20", {"entities" : qUnion([Q0, Q1, Q2, Q3, Q4, Q5, Q6, Q7, Q8, Q9]), "depth" : 60 * mm, "offsetDistance" : 25 * mm});
        }
        {
            var Q0;
            Q0=makeQuery(id+"F1.opExtrude","CAP_FACE",FACE,{"disambiguationData":[OSD([sQuery(id+"F0.wireOp",EDGE,"E0"),sQuery(id+"F0.wireOp",EDGE,"E1"),sQuery(id+"F0.wireOp",EDGE,"E2.1.0"),sQuery(id+"F0.wireOp",EDGE,"E2.2.0"),sQuery(id+"F0.wireOp",EDGE,"E2.3.0"),sQuery(id+"F0.wireOp",EDGE,"E2.4.0"),sQuery(id+"F0.wireOp",EDGE,"E2.5.0"),sQuery(id+"F0.wireOp",EDGE,"E2.6.0"),sQuery(id+"F0.wireOp",EDGE,"E2.7.0"),sQuery(id+"F0.wireOp",EDGE,"E3")])],"isStart":true});
            var sketch = newSketch(context, id + "F21", { "sketchPlane" : qUnion([Q0])});
            skCircle(sketch, "E69", {"center": v(425, 0) * mm, "radius": 10 * mm});
            skLineSegment(sketch, "E70.bottom", {"start": v(445, -20) * mm, "end": v(405, -20) * mm});
            skLineSegment(sketch, "E70.top", {"start": v(445, 20) * mm, "end": v(405, 20) * mm});
            skLineSegment(sketch, "E70.left", {"start": v(445, -20) * mm, "end": v(445, 20) * mm});
            skLineSegment(sketch, "E70.right", {"start": v(405, -20) * mm, "end": v(405, 20) * mm});
            skLineSegment(sketch, "E71.top", {"start": v(445, -60) * mm, "end": v(405, -60) * mm});
            skLineSegment(sketch, "E71.left", {"start": v(445, -20) * mm, "end": v(445, -60) * mm});
            skLineSegment(sketch, "E71.right", {"start": v(405, -20) * mm, "end": v(405, -60) * mm});
            skSolve(sketch);
        }
        {
            var Q0;
            Q0 = qSketchRegion(id + "F21", true);
            extrude(context, id + "F22", {"entities" : qUnion([Q0]), "depth" : 22 * mm, "offsetDistance" : 25 * mm, "hasSecondDirection" : true, "secondDirectionOppositeDirection" : false, "secondDirectionDepth" : 10 * mm});
        }
        {
            var Q0;
            Q0=makeQuery(id+"F21.imprint","IMPRINT",FACE,{"disambiguationData":[TD([[makeQuery(id+"F21.imprint","IMPRINT",EDGE,{"derivedFrom":sQuery(id+"F21.wireOp",EDGE,"E70.bottom")}),1.0]])]});
            var Q1;
            Q1=makeQuery(id+"F19.opExtrude","CAP_FACE",FACE,{"disambiguationData":[OSD([sQuery(id+"F18.wireOp",EDGE,"E45.bottom"),sQuery(id+"F18.wireOp",EDGE,"E45.top"),sQuery(id+"F18.wireOp",EDGE,"E45.left"),sQuery(id+"F18.wireOp",EDGE,"E45.right"),sQuery(id+"F18.wireOp",EDGE,"E46.0"),sQuery(id+"F18.wireOp",EDGE,"E46.1"),sQuery(id+"F18.wireOp",EDGE,"E58"),sQuery(id+"F18.wireOp",EDGE,"E59.0"),sQuery(id+"F18.wireOp",EDGE,"E60.1.0"),sQuery(id+"F18.wireOp",EDGE,"E60.1.1"),sQuery(id+"F18.wireOp",EDGE,"E60.2.0"),sQuery(id+"F18.wireOp",EDGE,"E60.2.1"),sQuery(id+"F18.wireOp",EDGE,"E60.3.0"),sQuery(id+"F18.wireOp",EDGE,"E60.3.1"),sQuery(id+"F18.wireOp",EDGE,"E62.trimOffspring"),sQuery(id+"F18.wireOp",EDGE,"E65.trimOffspring")])],"isStart":false});
            var Q2;
            Q2=makeQuery(id+"F19.opExtrude","CAP_FACE",FACE,{"disambiguationData":[OSD([sQuery(id+"F18.wireOp",EDGE,"E45.bottom"),sQuery(id+"F18.wireOp",EDGE,"E45.top"),sQuery(id+"F18.wireOp",EDGE,"E45.left"),sQuery(id+"F18.wireOp",EDGE,"E45.right"),sQuery(id+"F18.wireOp",EDGE,"E46.0"),sQuery(id+"F18.wireOp",EDGE,"E46.1"),sQuery(id+"F18.wireOp",EDGE,"E58"),sQuery(id+"F18.wireOp",EDGE,"E59.0"),sQuery(id+"F18.wireOp",EDGE,"E60.1.0"),sQuery(id+"F18.wireOp",EDGE,"E60.1.1"),sQuery(id+"F18.wireOp",EDGE,"E60.2.0"),sQuery(id+"F18.wireOp",EDGE,"E60.2.1"),sQuery(id+"F18.wireOp",EDGE,"E60.3.0"),sQuery(id+"F18.wireOp",EDGE,"E60.3.1"),sQuery(id+"F18.wireOp",EDGE,"E62.trimOffspring"),sQuery(id+"F18.wireOp",EDGE,"E65.trimOffspring")])],"isStart":false});
            extrude(context, id + "F23", {"entities" : qUnion([Q0]), "endBound" : BoundingType.UP_TO_SURFACE, "depth" : 22 * mm, "endBoundEntityFace" : qUnion([Q1]), "offsetDistance" : 25 * mm, "hasSecondDirection" : true, "secondDirectionOppositeDirection" : false, "secondDirectionDepth" : 22 * mm, "secondDirectionBoundEntityFace" : qUnion([Q2])});
        }
        {
            var Q0;
            {var subQ0=sQuery(id+"F21.wireOp",EDGE,"E71.right");Q0=makeQuery(id+"F23.boolean.opBoolean","MERGE",FACE,{"derivedFrom":[makeQuery(id+"F22.opExtrude","SWEPT_FACE",FACE,{"disambiguationData":[OSD([sQuery(id+"F21.wireOp",EDGE,"E70.right"),subQ0])]}),makeQuery(id+"F23.opExtrude","SWEPT_FACE",FACE,{"disambiguationData":[OSD([subQ0])]})]});}
            var sketch = newSketch(context, id + "F24", { "sketchPlane" : qUnion([Q0])});
            skLineSegment(sketch, "E72.bottom", {"start": v(-20, -148.5) * mm, "end": v(-60, -148.5) * mm});
            skLineSegment(sketch, "E72.top", {"start": v(-20, -68.5) * mm, "end": v(-60, -68.5) * mm});
            skLineSegment(sketch, "E72.left", {"start": v(-20, -148.5) * mm, "end": v(-20, -68.5) * mm});
            skLineSegment(sketch, "E72.right", {"start": v(-60, -148.5) * mm, "end": v(-60, -68.5) * mm});
            skSolve(sketch);
        }
        {
            var Q0;
            Q0 = qSketchRegion(id + "F24", true);
            extrude(context, id + "F25", {"entities" : qUnion([Q0]), "depth" : 25 * mm, "offsetDistance" : 25 * mm});
        }
        {
            var Q0;
            Q0=makeQuery(id+"F23.opExtrude","SWEPT_BODY",BODY,{"disambiguationData":[OSD([sQuery(id+"F21.wireOp",EDGE,"E70.bottom"),sQuery(id+"F21.wireOp",EDGE,"E71.top"),sQuery(id+"F21.wireOp",EDGE,"E71.left"),sQuery(id+"F21.wireOp",EDGE,"E71.right")])]});
            var Q1;
            Q1=makeQuery(id+"F25.opExtrude","SWEPT_BODY",BODY,{"disambiguationData":[OSD([sQuery(id+"F24.wireOp",EDGE,"E72.bottom"),sQuery(id+"F24.wireOp",EDGE,"E72.top"),sQuery(id+"F24.wireOp",EDGE,"E72.left"),sQuery(id+"F24.wireOp",EDGE,"E72.right")])]});
            var Q2;
            Q2=makeQuery(id+"F22.opExtrude","SWEPT_BODY",BODY,{"disambiguationData":[OSD([sQuery(id+"F21.wireOp",EDGE,"E69"),sQuery(id+"F21.wireOp",EDGE,"E70.top"),sQuery(id+"F21.wireOp",EDGE,"E70.left"),sQuery(id+"F21.wireOp",EDGE,"E70.right"),sQuery(id+"F21.wireOp",EDGE,"E71.top"),sQuery(id+"F21.wireOp",EDGE,"E71.left"),sQuery(id+"F21.wireOp",EDGE,"E71.right")])]});
            var Q3;
            Q3=makeQuery(id+"F8.opRevolve","SWEPT_FACE",FACE,{"disambiguationData":[OSD([sQuery(id+"F7.wireOp",EDGE,"E22")])]});
            circularPattern(context, id + "F26", {"entities" : qUnion([Q0, Q1, Q2]), "axis" : qUnion([Q3]), "angle" : 360 * degree, "instanceCount" : 2, "equalSpace" : true});
        }
        {
            var Q0;
            Q0=makeQuery(id+"F21.imprint","IMPRINT",FACE,{"disambiguationData":[TD([[makeQuery(id+"F21.imprint","IMPRINT",EDGE,{"derivedFrom":sQuery(id+"F21.wireOp",EDGE,"E70.top")}),-1.0]])]});
            cPlane(context, id + "F27", {"entities" : qUnion([Q0]), "cplaneType" : CPlaneType.OFFSET, "offset" : 35 * mm, "width" : 150 * mm, "height" : 150 * mm});
        }
        {
            var Q0;
            Q0=qCreatedBy(id+"F27.planeOp",FACE);
            var sketch = newSketch(context, id + "F28", { "sketchPlane" : qUnion([Q0])});
            skLineSegment(sketch, "E73", {"start": v(0, 347.42) * mm, "end": v(0, 410.69) * mm});
            skLineSegment(sketch, "E74", {"start": v(-5, 379.49) * mm, "end": v(-11, 379.49) * mm});
            skLineSegment(sketch, "E75", {"start": v(-11, 379.49) * mm, "end": v(-11, 376.49) * mm});
            skLineSegment(sketch, "E76", {"start": v(-11, 376.49) * mm, "end": v(-8.45, 376.49) * mm});
            skLineSegment(sketch, "E77", {"start": v(-8.45, 376.49) * mm, "end": v(-8.45, 371.49) * mm});
            skLineSegment(sketch, "E78", {"start": v(-8.45, 371.49) * mm, "end": v(-5, 371.49) * mm});
            skLineSegment(sketch, "E79", {"start": v(-5, 371.49) * mm, "end": v(-5, 379.49) * mm});
            skLineSegment(sketch, "E80", {"start": v(-14.77, 369.49) * mm, "end": v(15.64, 369.49) * mm});
            skLineSegment(sketch, "E81.MirrorCS", {"start": v(-8.45, 367.49) * mm, "end": v(-5, 367.49) * mm});
            skLineSegment(sketch, "E82.MirrorCS", {"start": v(-5, 367.49) * mm, "end": v(-5, 359.49) * mm});
            skLineSegment(sketch, "E83.MirrorCS", {"start": v(-5, 359.49) * mm, "end": v(-11, 359.49) * mm});
            skLineSegment(sketch, "E84.MirrorCS", {"start": v(-11, 359.49) * mm, "end": v(-11, 362.49) * mm});
            skLineSegment(sketch, "E85.MirrorCS", {"start": v(-8.45, 362.49) * mm, "end": v(-8.45, 367.49) * mm});
            skLineSegment(sketch, "E86.MirrorCS", {"start": v(-11, 362.49) * mm, "end": v(-8.45, 362.49) * mm});
            skSolve(sketch);
        }
        {
            var Q0;
            Q0=makeQuery(id+"F28.imprint","IMPRINT",FACE,{"disambiguationData":[TD([[makeQuery(id+"F28.imprint","IMPRINT",EDGE,{"derivedFrom":sQuery(id+"F28.wireOp",EDGE,"E74")}),1.0]])]});
            var Q1;
            Q1=makeQuery(id+"F28.imprint","IMPRINT",FACE,{"disambiguationData":[TD([[makeQuery(id+"F28.imprint","IMPRINT",EDGE,{"derivedFrom":sQuery(id+"F28.wireOp",EDGE,"E81.MirrorCS")}),-1.0]])]});
            var Q2;
            Q2=sQuery(id+"F28.wireOp",EDGE,"E73");
            var Q3;
            Q3=sQuery(id+"F28.wireOp",EDGE,"E73");
            revolve(context, id + "F29", {"entities" : qUnion([Q0, Q1]), "surfaceEntities" : qUnion([Q2]), "axis" : qUnion([Q3]), "revolveType" : RevolveType.FULL});
        }
        {
            var Q0;
            Q0=makeQuery(id+"F28.imprint","IMPRINT",FACE,{"disambiguationData":[TD([[makeQuery(id+"F28.imprint","IMPRINT",EDGE,{"derivedFrom":sQuery(id+"F28.wireOp",EDGE,"E74")}),1.0]])]});
            var Q1;
            Q1=sQuery(id+"F28.wireOp",EDGE,"E73");
            revolve(context, id + "F30", {"entities" : qUnion([Q0]), "axis" : qUnion([Q1]), "revolveType" : RevolveType.FULL});
        }
        {
            var Q0;
            Q0=makeQuery(id+"F29.opRevolve","SWEPT_BODY",BODY,{"disambiguationData":[OSD([sQuery(id+"F28.wireOp",EDGE,"E74"),sQuery(id+"F28.wireOp",EDGE,"E75"),sQuery(id+"F28.wireOp",EDGE,"E76"),sQuery(id+"F28.wireOp",EDGE,"E77"),sQuery(id+"F28.wireOp",EDGE,"E78"),sQuery(id+"F28.wireOp",EDGE,"E79")])]});
            var Q1;
            Q1=makeQuery(id+"F29.opRevolve","SWEPT_BODY",BODY,{"disambiguationData":[OSD([sQuery(id+"F28.wireOp",EDGE,"E81.MirrorCS"),sQuery(id+"F28.wireOp",EDGE,"E82.MirrorCS"),sQuery(id+"F28.wireOp",EDGE,"E83.MirrorCS"),sQuery(id+"F28.wireOp",EDGE,"E84.MirrorCS"),sQuery(id+"F28.wireOp",EDGE,"E86.MirrorCS"),sQuery(id+"F28.wireOp",EDGE,"E85.MirrorCS")])]});
            var Q2;
            Q2=makeQuery(id+"F8.opRevolve","SWEPT_EDGE",EDGE,{"disambiguationData":[OSD([sQuery(id+"F7.wireOp",EDGE,"E21"),sQuery(id+"F7.wireOp",EDGE,"E26")])]});
            circularPattern(context, id + "F31", {"entities" : qUnion([Q0, Q1]), "axis" : qUnion([Q2]), "angle" : 360 * degree, "instanceCount" : 5, "equalSpace" : true});
        }
    });
